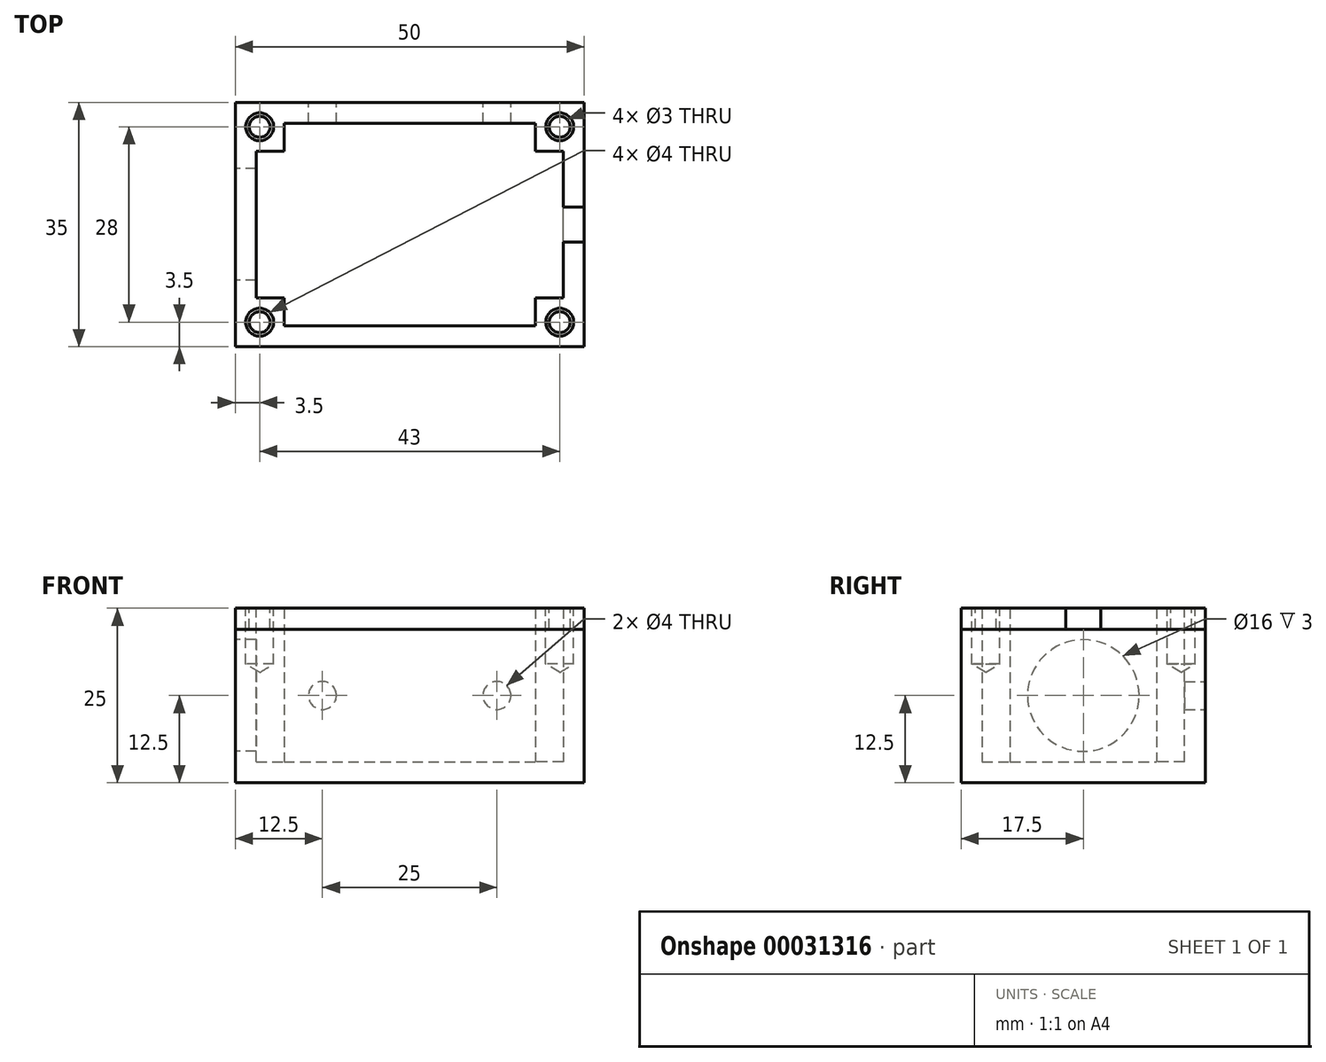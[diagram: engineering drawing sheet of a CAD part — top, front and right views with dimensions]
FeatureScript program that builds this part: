
annotation { "Feature Type Name" : "Feature", "Feature Type Description" : "" }
export const myFeature = defineFeature(function(context is Context, id is Id, definition is map)
    precondition{}
    {
        {
            var Q0;
            Q0=qCreatedBy(makeId("Top.planeOp"),FACE);
            var sketch = newSketch(context, id + "F0", { "sketchPlane" : qUnion([Q0])});
            skLineSegment(sketch, "E0.bottom", {"start": v(0, 0) * mm, "end": v(50, 0) * mm});
            skLineSegment(sketch, "E0.top", {"start": v(0, 35) * mm, "end": v(50, 35) * mm});
            skLineSegment(sketch, "E0.left", {"start": v(0, 0) * mm, "end": v(0, 35) * mm});
            skLineSegment(sketch, "E0.right", {"start": v(50, 0) * mm, "end": v(50, 35) * mm});
            skSolve(sketch);
        }
        {
            var Q0;
            Q0=makeQuery(id+"F0.imprint","IMPRINT",FACE,{"disambiguationData":[TD([[makeQuery(id+"F0.imprint","IMPRINT",EDGE,{"derivedFrom":sQuery(id+"F0.wireOp",EDGE,"E0.bottom")}),1.0]])]});
            extrude(context, id + "F1", {"entities" : qUnion([Q0]), "depth" : 25 * mm});
        }
        {
            var Q0;
            Q0=makeQuery(id+"F1.opExtrude","CAP_FACE",FACE,{"disambiguationData":[OSD([sQuery(id+"F0.wireOp",EDGE,"E0.bottom"),sQuery(id+"F0.wireOp",EDGE,"E0.top"),sQuery(id+"F0.wireOp",EDGE,"E0.left"),sQuery(id+"F0.wireOp",EDGE,"E0.right")])],"isStart":false});
            shell(context, id + "F2", {"entities" : qUnion([Q0]), "thickness" : 3 * mm});
        }
        {
            var Q0;
            Q0=makeQuery(id+"F1.opExtrude","CAP_FACE",FACE,{"disambiguationData":[OSD([sQuery(id+"F0.wireOp",EDGE,"E0.bottom"),sQuery(id+"F0.wireOp",EDGE,"E0.top"),sQuery(id+"F0.wireOp",EDGE,"E0.left"),sQuery(id+"F0.wireOp",EDGE,"E0.right")])],"isStart":false});
            var sketch = newSketch(context, id + "F3", { "sketchPlane" : qUnion([Q0])});
            skLineSegment(sketch, "E1.bottom", {"start": v(0, 0) * mm, "end": v(7, 0) * mm});
            skLineSegment(sketch, "E1.top", {"start": v(0, 7) * mm, "end": v(7, 7) * mm});
            skLineSegment(sketch, "E1.left", {"start": v(0, 0) * mm, "end": v(0, 7) * mm});
            skLineSegment(sketch, "E1.right", {"start": v(7, 0) * mm, "end": v(7, 7) * mm});
            skLineSegment(sketch, "E2.bottom", {"start": v(0, 35) * mm, "end": v(7, 35) * mm});
            skLineSegment(sketch, "E2.top", {"start": v(0, 28) * mm, "end": v(7, 28) * mm});
            skLineSegment(sketch, "E2.left", {"start": v(0, 35) * mm, "end": v(0, 28) * mm});
            skLineSegment(sketch, "E2.right", {"start": v(7, 35) * mm, "end": v(7, 28) * mm});
            skLineSegment(sketch, "E3.bottom", {"start": v(50, 35) * mm, "end": v(43, 35) * mm});
            skLineSegment(sketch, "E3.top", {"start": v(50, 28) * mm, "end": v(43, 28) * mm});
            skLineSegment(sketch, "E3.left", {"start": v(50, 35) * mm, "end": v(50, 28) * mm});
            skLineSegment(sketch, "E3.right", {"start": v(43, 35) * mm, "end": v(43, 28) * mm});
            skLineSegment(sketch, "E4.bottom", {"start": v(50, 0) * mm, "end": v(43, 0) * mm});
            skLineSegment(sketch, "E4.top", {"start": v(50, 7) * mm, "end": v(43, 7) * mm});
            skLineSegment(sketch, "E4.left", {"start": v(50, 0) * mm, "end": v(50, 7) * mm});
            skLineSegment(sketch, "E4.right", {"start": v(43, 0) * mm, "end": v(43, 7) * mm});
            skSolve(sketch);
        }
        {
            var Q0;
            Q0 = qSketchRegion(id + "F3", true);
            extrude(context, id + "F4", {"entities" : qUnion([Q0]), "operationType" : NewBodyOperationType.ADD, "oppositeDirection" : true, "depth" : 25 * mm});
        }
        {
            var Q0;
            Q0=makeQuery(id+"F4.boolean.opBoolean","MERGE",FACE,{"derivedFrom":[makeQuery(id+"F1.opExtrude","CAP_FACE",FACE,{"disambiguationData":[OSD([sQuery(id+"F0.wireOp",EDGE,"E0.bottom"),sQuery(id+"F0.wireOp",EDGE,"E0.top"),sQuery(id+"F0.wireOp",EDGE,"E0.left"),sQuery(id+"F0.wireOp",EDGE,"E0.right")])],"isStart":false}),makeQuery(id+"F4.opExtrude","CAP_FACE",FACE,{"disambiguationData":[OSD([sQuery(id+"F3.wireOp",EDGE,"E1.bottom"),sQuery(id+"F3.wireOp",EDGE,"E1.top"),sQuery(id+"F3.wireOp",EDGE,"E1.left"),sQuery(id+"F3.wireOp",EDGE,"E1.right")])],"isStart":true}),makeQuery(id+"F4.opExtrude","CAP_FACE",FACE,{"disambiguationData":[OSD([sQuery(id+"F3.wireOp",EDGE,"E2.bottom"),sQuery(id+"F3.wireOp",EDGE,"E2.top"),sQuery(id+"F3.wireOp",EDGE,"E2.left"),sQuery(id+"F3.wireOp",EDGE,"E2.right")])],"isStart":true}),makeQuery(id+"F4.opExtrude","CAP_FACE",FACE,{"disambiguationData":[OSD([sQuery(id+"F3.wireOp",EDGE,"E3.bottom"),sQuery(id+"F3.wireOp",EDGE,"E3.top"),sQuery(id+"F3.wireOp",EDGE,"E3.left"),sQuery(id+"F3.wireOp",EDGE,"E3.right")])],"isStart":true}),makeQuery(id+"F4.opExtrude","CAP_FACE",FACE,{"disambiguationData":[OSD([sQuery(id+"F3.wireOp",EDGE,"E4.bottom"),sQuery(id+"F3.wireOp",EDGE,"E4.top"),sQuery(id+"F3.wireOp",EDGE,"E4.left"),sQuery(id+"F3.wireOp",EDGE,"E4.right")])],"isStart":true})]});
            var sketch = newSketch(context, id + "F5", { "sketchPlane" : qUnion([Q0])});
            skCircle(sketch, "E5", {"center": v(3.5, 31.5) * mm, "radius": 2 * mm});
            skLineSegment(sketch, "E6", {"start": v(0, 35) * mm, "end": v(7, 28) * mm});
            skCircle(sketch, "E7", {"center": v(46.5, 31.5) * mm, "radius": 2 * mm});
            skCircle(sketch, "E8", {"center": v(46.5, 3.5) * mm, "radius": 2 * mm});
            skCircle(sketch, "E9", {"center": v(3.5, 3.5) * mm, "radius": 2 * mm});
            skLineSegment(sketch, "E10", {"start": v(0, 0) * mm, "end": v(7, 7) * mm});
            skLineSegment(sketch, "E11", {"start": v(43, 7) * mm, "end": v(50, 0) * mm});
            skLineSegment(sketch, "E12", {"start": v(50, 35) * mm, "end": v(43, 28) * mm});
            skSolve(sketch);
        }
        {
            var Q0;
            Q0=sQuery(id+"F5.wireOp",VERTEX,"E9.center");
            var Q1;
            Q1=sQuery(id+"F5.wireOp",VERTEX,"E8.center");
            var Q2;
            Q2=sQuery(id+"F5.wireOp",VERTEX,"E7.center");
            var Q3;
            Q3=sQuery(id+"F5.wireOp",VERTEX,"E5.center");
            var Q4;
            Q4=makeQuery(id+"F1.opExtrude","SWEPT_BODY",BODY,{"disambiguationData":[OSD([sQuery(id+"F0.wireOp",EDGE,"E0.bottom"),sQuery(id+"F0.wireOp",EDGE,"E0.top"),sQuery(id+"F0.wireOp",EDGE,"E0.left"),sQuery(id+"F0.wireOp",EDGE,"E0.right")])]});
            hole(context, id + "F6", {"style" : HoleStyle.SIMPLE, "holeDiameter" : 4 * mm, "endStyle" : HoleEndStyle.BLIND, "holeDepth" : 8 * mm, "locations" : qUnion([Q0, Q1, Q2, Q3]), "scope" : qUnion([Q4])});
        }
        {
            var Q0;
            Q0=makeQuery(id+"F1.opExtrude","SWEPT_FACE",FACE,{"disambiguationData":[OSD([sQuery(id+"F0.wireOp",EDGE,"E0.left")])]});
            var sketch = newSketch(context, id + "F7", { "sketchPlane" : qUnion([Q0])});
            skLineSegment(sketch, "E13", {"start": v(-35, 0) * mm, "end": v(0, 25) * mm});
            skCircle(sketch, "E14", {"center": v(-17.5, 12.5) * mm, "radius": 8 * mm});
            skSolve(sketch);
        }
        {
            var Q0;
            Q0=sQuery(id+"F7.wireOp",VERTEX,"E14.center");
            var Q1;
            Q1=makeQuery(id+"F1.opExtrude","SWEPT_BODY",BODY,{"disambiguationData":[OSD([sQuery(id+"F0.wireOp",EDGE,"E0.bottom"),sQuery(id+"F0.wireOp",EDGE,"E0.top"),sQuery(id+"F0.wireOp",EDGE,"E0.left"),sQuery(id+"F0.wireOp",EDGE,"E0.right")])]});
            hole(context, id + "F8", {"style" : HoleStyle.SIMPLE, "holeDiameter" : 16 * mm, "endStyle" : HoleEndStyle.BLIND, "holeDepth" : 20 * mm, "locations" : qUnion([Q0]), "scope" : qUnion([Q1])});
        }
        {
            var Q0;
            Q0=makeQuery(id+"F1.opExtrude","SWEPT_FACE",FACE,{"disambiguationData":[OSD([sQuery(id+"F0.wireOp",EDGE,"E0.right")])]});
            var sketch = newSketch(context, id + "F9", { "sketchPlane" : qUnion([Q0])});
            skPoint(sketch, "E15", {"position": v(17.5, 25) * mm});
            skLineSegment(sketch, "E16.rect.bottom", {"start": v(20, 22) * mm, "end": v(15, 22) * mm});
            skLineSegment(sketch, "E16.rect.top", {"start": v(20, 28) * mm, "end": v(15, 28) * mm});
            skLineSegment(sketch, "E16.rect.left", {"start": v(20, 22) * mm, "end": v(20, 28) * mm});
            skLineSegment(sketch, "E16.rect.right", {"start": v(15, 22) * mm, "end": v(15, 28) * mm});
            skSolve(sketch);
        }
        {
            var Q0;
            Q0 = qSketchRegion(id + "F9", true);
            extrude(context, id + "F10", {"entities" : qUnion([Q0]), "operationType" : NewBodyOperationType.REMOVE, "oppositeDirection" : true, "depth" : 25 * mm});
        }
        {
            var Q0;
            Q0=makeQuery(id+"F1.opExtrude","SWEPT_FACE",FACE,{"disambiguationData":[OSD([sQuery(id+"F0.wireOp",EDGE,"E0.top")])]});
            var sketch = newSketch(context, id + "F11", { "sketchPlane" : qUnion([Q0])});
            skPoint(sketch, "E17", {"position": v(-50, 12.5) * mm});
            skPoint(sketch, "E18", {"position": v(0, 12.5) * mm});
            skLineSegment(sketch, "E19", {"start": v(-50, 12.5) * mm, "end": v(0, 12.5) * mm});
            skPoint(sketch, "E20", {"position": v(-25, 12.5) * mm});
            skLineSegment(sketch, "E21", {"start": v(-50, 12.5) * mm, "end": v(-25, 12.5) * mm});
            skPoint(sketch, "E22", {"position": v(-37.5, 12.5) * mm});
            skLineSegment(sketch, "E23", {"start": v(-25, 12.5) * mm, "end": v(0, 12.5) * mm});
            skPoint(sketch, "E24", {"position": v(-12.5, 12.5) * mm});
            skSolve(sketch);
        }
        {
            var Q0;
            Q0=sQuery(id+"F11.wireOp",VERTEX,"E22");
            var Q1;
            Q1=makeQuery(id+"F1.opExtrude","SWEPT_BODY",BODY,{"disambiguationData":[OSD([sQuery(id+"F0.wireOp",EDGE,"E0.bottom"),sQuery(id+"F0.wireOp",EDGE,"E0.top"),sQuery(id+"F0.wireOp",EDGE,"E0.left"),sQuery(id+"F0.wireOp",EDGE,"E0.right")])]});
            hole(context, id + "F12", {"style" : HoleStyle.SIMPLE, "holeDiameter" : 4 * mm, "endStyle" : HoleEndStyle.BLIND, "holeDepth" : 6 * mm, "locations" : qUnion([Q0]), "scope" : qUnion([Q1])});
        }
        {
            var Q0;
            Q0=sQuery(id+"F11.wireOp",VERTEX,"E24");
            var Q1;
            Q1=makeQuery(id+"F1.opExtrude","SWEPT_BODY",BODY,{"disambiguationData":[OSD([sQuery(id+"F0.wireOp",EDGE,"E0.bottom"),sQuery(id+"F0.wireOp",EDGE,"E0.top"),sQuery(id+"F0.wireOp",EDGE,"E0.left"),sQuery(id+"F0.wireOp",EDGE,"E0.right")])]});
            hole(context, id + "F13", {"style" : HoleStyle.SIMPLE, "holeDiameter" : 4 * mm, "endStyle" : HoleEndStyle.BLIND, "holeDepth" : 6 * mm, "locations" : qUnion([Q0]), "scope" : qUnion([Q1])});
        }
        {
            var Q0;
            Q0=makeQuery(id+"F4.boolean.opBoolean","MERGE",FACE,{"derivedFrom":[makeQuery(id+"F1.opExtrude","CAP_FACE",FACE,{"disambiguationData":[OSD([sQuery(id+"F0.wireOp",EDGE,"E0.bottom"),sQuery(id+"F0.wireOp",EDGE,"E0.top"),sQuery(id+"F0.wireOp",EDGE,"E0.left"),sQuery(id+"F0.wireOp",EDGE,"E0.right")])],"isStart":false}),makeQuery(id+"F4.opExtrude","CAP_FACE",FACE,{"disambiguationData":[OSD([sQuery(id+"F3.wireOp",EDGE,"E1.bottom"),sQuery(id+"F3.wireOp",EDGE,"E1.top"),sQuery(id+"F3.wireOp",EDGE,"E1.left"),sQuery(id+"F3.wireOp",EDGE,"E1.right")])],"isStart":true}),makeQuery(id+"F4.opExtrude","CAP_FACE",FACE,{"disambiguationData":[OSD([sQuery(id+"F3.wireOp",EDGE,"E2.bottom"),sQuery(id+"F3.wireOp",EDGE,"E2.top"),sQuery(id+"F3.wireOp",EDGE,"E2.left"),sQuery(id+"F3.wireOp",EDGE,"E2.right")])],"isStart":true}),makeQuery(id+"F4.opExtrude","CAP_FACE",FACE,{"disambiguationData":[OSD([sQuery(id+"F3.wireOp",EDGE,"E3.bottom"),sQuery(id+"F3.wireOp",EDGE,"E3.top"),sQuery(id+"F3.wireOp",EDGE,"E3.left"),sQuery(id+"F3.wireOp",EDGE,"E3.right")])],"isStart":true}),makeQuery(id+"F4.opExtrude","CAP_FACE",FACE,{"disambiguationData":[OSD([sQuery(id+"F3.wireOp",EDGE,"E4.bottom"),sQuery(id+"F3.wireOp",EDGE,"E4.top"),sQuery(id+"F3.wireOp",EDGE,"E4.left"),sQuery(id+"F3.wireOp",EDGE,"E4.right")])],"isStart":true})]});
            var sketch = newSketch(context, id + "F14", { "sketchPlane" : qUnion([Q0])});
            skLineSegment(sketch, "E25.bottom", {"start": v(0, 0) * mm, "end": v(50, 0) * mm});
            skLineSegment(sketch, "E25.top", {"start": v(0, 35) * mm, "end": v(50, 35) * mm});
            skLineSegment(sketch, "E25.left", {"start": v(0, 0) * mm, "end": v(0, 35) * mm});
            skLineSegment(sketch, "E25.right", {"start": v(50, 0) * mm, "end": v(50, 35) * mm});
            skCircle(sketch, "E26", {"center": v(3.5, 31.5) * mm, "radius": 1.5 * mm});
            skCircle(sketch, "E27", {"center": v(3.5, 3.5) * mm, "radius": 1.5 * mm});
            skCircle(sketch, "E28", {"center": v(46.5, 31.5) * mm, "radius": 1.5 * mm});
            skCircle(sketch, "E29", {"center": v(46.5, 3.5) * mm, "radius": 1.5 * mm});
            skSolve(sketch);
        }
        {
            var Q0;
            Q0 = qSketchRegion(id + "F14", true);
            extrude(context, id + "F15", {"entities" : qUnion([Q0]), "oppositeDirection" : true, "depth" : 3 * mm});
        }
    });
